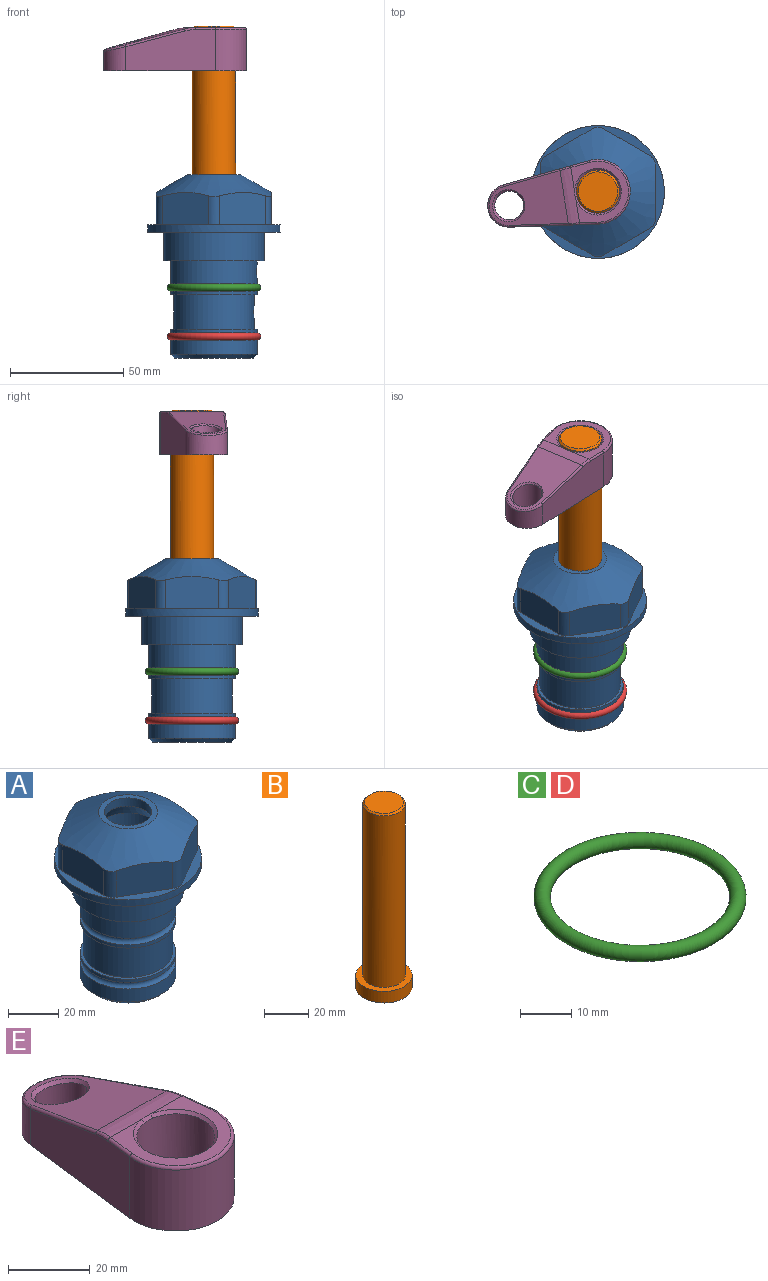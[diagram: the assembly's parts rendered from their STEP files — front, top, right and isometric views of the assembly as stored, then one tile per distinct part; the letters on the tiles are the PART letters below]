
ASSEMBLY  parts=5 mates=4
PART A: 36 faces, bbox 58.7x58.7x81 mm
  f0: cylinder r=17.78mm len=35.56mm, axis (0,0,1), area 1670.8mm2, adj f23,f24,f31
  f1: cylinder r=19.05mm len=38.1mm, axis (0,0,1), area 1191.9mm2, adj f26,f27,f30
  f2: plane 58.66x58.66mm, normal (0,0,-1), area 1150.6mm2, adj f3,f28
  f3: cylinder r=29.33mm len=58.66mm, axis (0,0,-1), area 585.1mm2, adj f2,f4
  f4: plane 58.66x58.66mm, normal (0,0,1), area 475.9mm2, adj f3,f5,f6,f7,f8,f9,f10,f11
  f5: plane 20.32x14.34mm, normal (-0.5,0.87,0), area 324.4mm2, adj f4,f15,f16,f17
  f6: plane 20.32x14.34mm, normal (0.5,0.87,0), area 324.4mm2, adj f4,f14,f15,f17
  f7: plane 23.48x14.34mm, normal (1,0,0), area 324.4mm2, adj f4,f13,f14,f17
  f8: plane 20.32x14.34mm, normal (0.5,-0.87,0), area 324.4mm2, adj f4,f12,f13,f17
  f9: plane 20.32x14.34mm, normal (-0.5,-0.87,0), area 324.4mm2, adj f4,f11,f12,f17
  f10: plane 23.48x14.34mm, normal (-1,0,0), area 324.4mm2, adj f4,f11,f16,f17
  f11: cylinder r=5.08mm len=12.85mm, axis (0,0,-1), area 67.2mm2, adj f4,f9,f10,f17
  f12: cylinder r=5.08mm len=12.85mm, axis (0,0,-1), area 67.2mm2, adj f4,f8,f9,f17
  f13: cylinder r=5.08mm len=12.85mm, axis (0,0,-1), area 67.2mm2, adj f4,f7,f8,f17
  f14: cylinder r=5.08mm len=12.85mm, axis (0,0,-1), area 67.2mm2, adj f4,f6,f7,f17
  f15: cylinder r=5.08mm len=12.85mm, axis (0,0,-1), area 67.2mm2, adj f4,f5,f6,f17
  f16: cylinder r=5.08mm len=12.85mm, axis (0,0,-1), area 67.2mm2, adj f4,f5,f10,f17
  f17: cone r=11.73mm half-angle=60deg, axis (0,0,-1), area 2071.8mm2, adj f5,f6,f7,f8,f9,f10,f11,f12
  f18: plane 23.46x23.46mm, normal (0,0,1), area 147.4mm2, adj f17,f35
  f19: plane 34.93x34.93mm, normal (0,0,-1), area 958mm2, adj f29
  f20: cylinder r=19.05mm len=38.1mm, axis (0,0,1), area 760.1mm2, adj f21,f29
  f21: torus R=19.05mm, axis (0,0,1), area 565.3mm2, adj f20,f22
  f22: cylinder r=19.05mm len=38.1mm, axis (0,0,1), area 190mm2, adj f21,f23
  f23: plane 38.1x38.1mm, normal (0,0,1), area 146.9mm2, adj f0,f22
  f24: plane 38.1x38.1mm, normal (0,0,-1), area 146.9mm2, adj f0,f25
  f25: cylinder r=19.05mm len=38.1mm, axis (0,0,1), area 190mm2, adj f24,f26
  f26: torus R=19.05mm, axis (0,0,1), area 565.3mm2, adj f1,f25
  f27: plane 44.45x44.45mm, normal (0,0,-1), area 411.7mm2, adj f1,f28
  f28: cylinder r=22.23mm len=44.45mm, axis (0,0,1), area 1773.5mm2, adj f2,f27
  f29: cone r=19.05mm half-angle=45deg, axis (0,0,1), area 257.5mm2, adj f19,f20
  f30: cylinder r=3.17mm len=6.75mm, axis (-1,0,0), area 128mm2, adj f1,f33
  f31: cylinder r=3.17mm len=6.35mm, axis (-1,0,0), area 102.5mm2, adj f0,f33
  f32: plane 25.4x25.4mm, normal (0,0,1), area 506.7mm2, adj f33
  f33: cylinder r=12.7mm len=66.42mm, axis (0,0,-1), area 5236.2mm2, adj f30,f31,f32,f34
  f34: cone r=9.53mm half-angle=30deg, axis (0,0,-1), area 443.4mm2, adj f33,f35
  f35: cylinder r=9.53mm len=19.05mm, axis (0,0,-1), area 240.9mm2, adj f18,f34
PART B: 6 faces, bbox 25.4x25.4x101.6 mm
  f0: plane 17.46x17.46mm, normal (0,0,1), area 239.5mm2, adj f5
  f1: plane 25.4x25.4mm, normal (0,0,-1), area 506.7mm2, adj f2
  f2: cylinder r=12.7mm len=25.4mm, axis (0,0,1), area 506.7mm2, adj f1,f3
  f3: plane 25.4x25.4mm, normal (0,0,1), area 221.7mm2, adj f2,f4
  f4: cylinder r=9.53mm len=94.46mm, axis (0,0,1), area 5653mm2, adj f3,f5
  f5: cone r=8.73mm half-angle=45deg, axis (0,0,-1), area 64.4mm2, adj f0,f4
PART C: 1 faces, bbox 44.7x44.7x3.2 mm
  f0: torus R=19.05mm, axis (0,0,1), area 1193.9mm2
PART D: same geometry as C
PART E: 31 faces, bbox 31.7x65.5x19.8 mm
  f0: plane 39.12x18.26mm, normal (0.99,0.12,0), area 612.2mm2, adj f1,f4,f7,f11,f13,f15
  f1: cylinder r=9.53mm len=18.91mm, axis (0,0,-1), area 296.1mm2, adj f0,f2,f7,f17
  f2: plane 39.12x18.26mm, normal (-0.99,0.12,0), area 612.2mm2, adj f1,f4,f7,f12,f14,f16
  f3: cylinder r=6.35mm len=12.7mm, axis (0,0,-1), area 362.4mm2, adj f7,f18
  f4: cylinder r=14.29mm len=28.58mm, axis (0,0,-1), area 882.2mm2, adj f0,f2,f7,f10
  f5: cylinder r=9.53mm len=19.05mm, axis (0,0,-1), area 1092.6mm2, adj f7,f19,f20
  f6: plane 26.99x23.69mm, normal (0,0,1), area 216.2mm2, adj f9,f10,f11,f12,f19
  f7: plane 63.5x28.58mm, normal (0,0,-1), area 661.8mm2, adj f0,f1,f2,f3,f4,f5,f22,f23
  f8: plane 33.52x23.6mm, normal (0,0.26,0.97), area 486mm2, adj f9,f15,f16,f17,f18
  f9: cylinder r=19.05mm len=24.72mm, axis (1,0,0), area 120.4mm2, adj f6,f8,f13,f14,f20
  f10: torus R=13.49mm, axis (0,0,1), area 59mm2, adj f4,f6,f11,f12
  f11: cylinder r=0.79mm len=8.67mm, axis (0.12,-0.99,0), area 10.8mm2, adj f0,f6,f10,f13
  f12: cylinder r=0.79mm len=8.67mm, axis (0.12,0.99,0), area 10.8mm2, adj f2,f6,f10,f14
  f13: bspline ~4.95x1.42mm, area 6.1mm2, adj f0,f9,f11,f15
  f14: bspline ~4.95x1.42mm, area 6.1mm2, adj f2,f9,f12,f16
  f15: cylinder r=0.79mm len=25.95mm, axis (0.12,-0.96,0.26), area 32.9mm2, adj f0,f8,f13,f17
  f16: cylinder r=0.79mm len=25.95mm, axis (0.12,0.96,-0.26), area 32.9mm2, adj f2,f8,f14,f17
  f17: bspline ~18.91x8.38mm, area 30mm2, adj f1,f8,f15,f16
  f18: bspline ~14.29x14.29mm, area 48.3mm2, adj f3,f8
  f19: cone r=9.53mm half-angle=45deg, axis (0,0,1), area 66.5mm2, adj f5,f6,f20
  f20: bspline ~3.22x0.96mm, area 3.5mm2, adj f5,f9,f19
  f21: plane 2.75x2.72mm, normal (0,0,-1), area 2.9mm2, adj f23,f25,f28
  f22: plane 23.05x15.88mm, normal (-0.99,-0.12,0), area 323.6mm2, adj f7,f25,f26,f27,f28,f29
  f23: plane 23.05x15.88mm, normal (0.99,-0.12,0), area 323.6mm2, adj f7,f21,f25,f27,f28,f30
  f24: cylinder r=9.53mm len=10.69mm, axis (0,0,-1), area 114.7mm2, adj f7,f27,f29,f30
  f25: cylinder r=12.7mm len=20.59mm, axis (0,0,-1), area 381.1mm2, adj f7,f21,f22,f23,f26,f28
  f26: plane 2.75x2.72mm, normal (0,0,-1), area 2.9mm2, adj f22,f25,f28
  f27: plane 19.72x18.37mm, normal (0,-0.26,-0.97), area 291.8mm2, adj f22,f23,f24,f28,f29,f30
  f28: cylinder r=15.88mm len=19.92mm, axis (1,0,0), area 54.8mm2, adj f21,f22,f23,f25,f26,f27
  f29: cylinder r=1.59mm len=11mm, axis (0,0,-1), area 34.7mm2, adj f7,f22,f24,f27
  f30: cylinder r=1.59mm len=11mm, axis (0,0,-1), area 34.7mm2, adj f7,f23,f24,f27
PLACE A at identity fixed
PLACE B rot(axis=(0,0,1),98.9deg) t=(0,0,27.55)mm
PLACE C at identity
PLACE D t=(0,0,-21.59)mm
PLACE E rot(axis=(0,0,1),98.9deg) t=(0,0,26.76)mm
MATE fastened C.f0 <-> A.f0  axis (0,0,1) through (0,0,-24.51)mm
MATE fastened B.f2 <-> E.f4  axis (0,0,1) through (0,0,90.26)mm
MATE cylindrical B.f2 <-> A.f0  axis (0,0,-1) through (0,0,-10.55)mm
MATE fastened D.f0 <-> A.f0  axis (0,0,1) through (0,0,-46.1)mm
